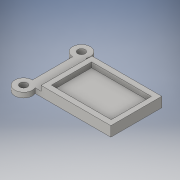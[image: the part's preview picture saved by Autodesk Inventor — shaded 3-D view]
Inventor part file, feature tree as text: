
AUTODESK INVENTOR PART (.ipt)
format: ipt  version: 2016 (Build 200138000, 138)  size: 125,952 bytes
history: native  units: in
note: dims shown in document units (in); Inventor stores cm internally (conversion verified against a paired STEP export)
features: extrude x2, sketch x2
ambient origin geometry x8: Origin, YZ Plane, XZ Plane, XY Plane, X Axis, Y Axis, Z Axis, Center Point
bodies: Solid1 (feature_tree)
feature tree (4):
  extrude  "Extrusion1"  Depth=0.37in
  extrude  "Extrusion2"  Depth=0.25in TaperAngle=0.0deg
  sketch  "Sketch1"  dims[d1=0.37in d2=0.37in]
  sketch  "Sketch2"  dims[d4=0.25in d5=0.25in d6=0.0in d7=0.25in d8=0.25in d9=0.0in]
